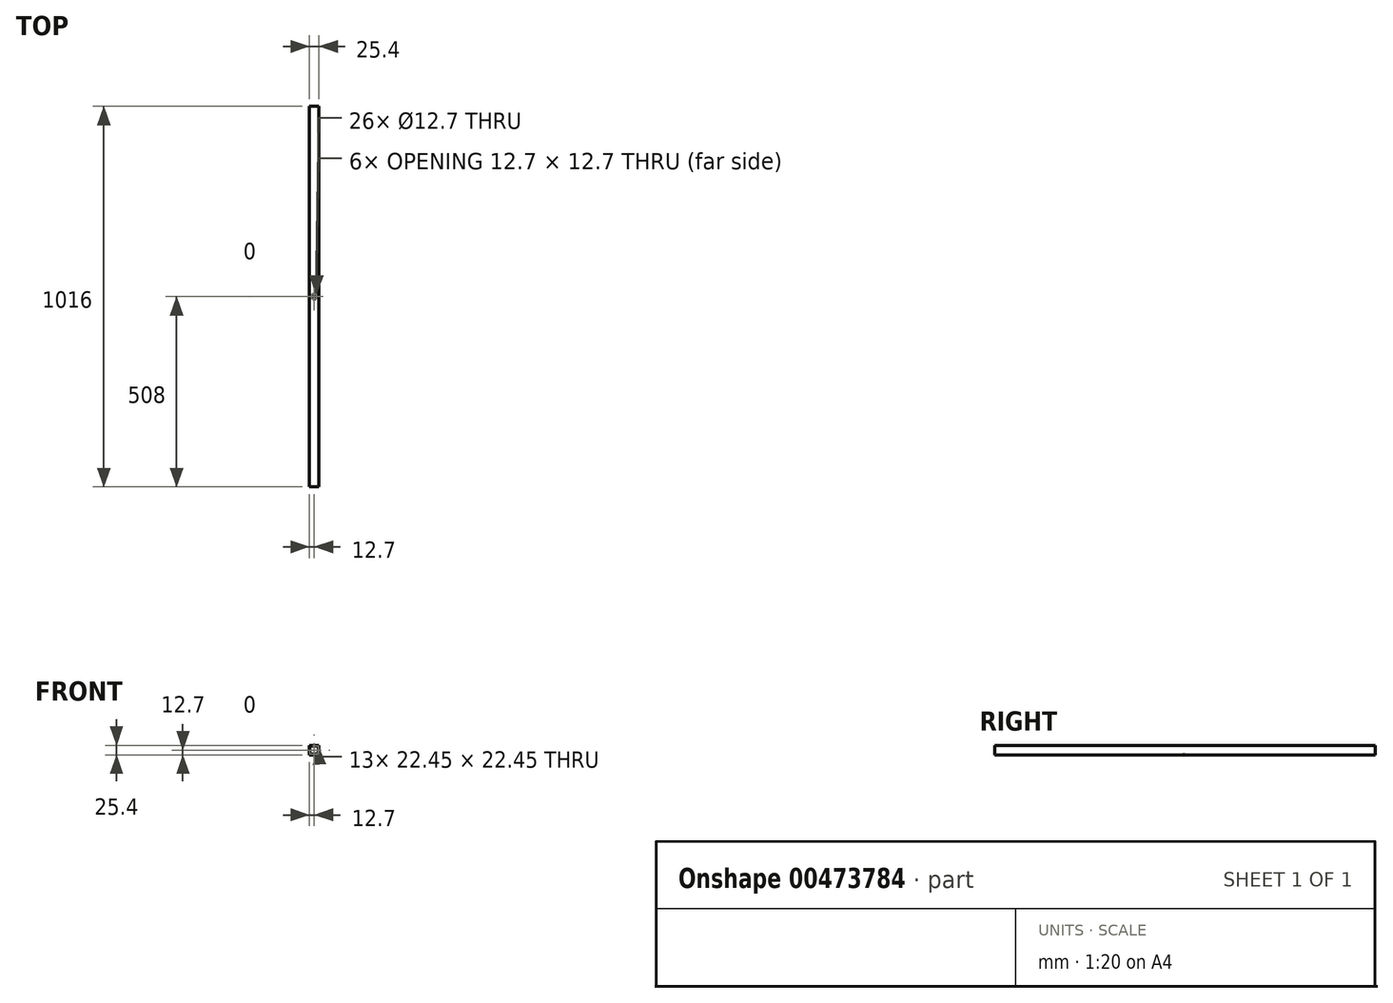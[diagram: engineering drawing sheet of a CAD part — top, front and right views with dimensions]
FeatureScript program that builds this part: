
annotation { "Feature Type Name" : "Feature", "Feature Type Description" : "" }
export const myFeature = defineFeature(function(context is Context, id is Id, definition is map)
    precondition{}
    {
        {
            var Q0;
            Q0=qCreatedBy(makeId("Front.planeOp"),FACE);
            var sketch = newSketch(context, id + "F0", { "sketchPlane" : qUnion([Q0])});
            skLineSegment(sketch, "E0.bottom", {"start": v(0, 0) * mm, "end": v(25.4, 0) * mm});
            skLineSegment(sketch, "E0.top", {"start": v(0, 25.4) * mm, "end": v(25.4, 25.4) * mm});
            skLineSegment(sketch, "E0.left", {"start": v(0, 0) * mm, "end": v(0, 25.4) * mm});
            skLineSegment(sketch, "E0.right", {"start": v(25.4, 0) * mm, "end": v(25.4, 25.4) * mm});
            skLineSegment(sketch, "E1.0", {"start": v(23.93, 1.47) * mm, "end": v(23.93, 23.93) * mm});
            skLineSegment(sketch, "E1.1", {"start": v(1.47, 1.47) * mm, "end": v(23.93, 1.47) * mm});
            skLineSegment(sketch, "E1.2", {"start": v(1.47, 1.47) * mm, "end": v(1.47, 23.93) * mm});
            skLineSegment(sketch, "E1.3", {"start": v(1.47, 23.93) * mm, "end": v(23.93, 23.93) * mm});
            skSolve(sketch);
        }
        {
            var Q0;
            Q0 = qSketchRegion(id + "F0", true);
            extrude(context, id + "F1", {"entities" : qUnion([Q0]), "depth" : 1016 * mm});
        }
        {
            var Q0;
            Q0=makeQuery(id+"F1.opExtrude","SWEPT_FACE",FACE,{"disambiguationData":[OSD([sQuery(id+"F0.wireOp",EDGE,"E0.bottom")])]});
            var sketch = newSketch(context, id + "F2", { "sketchPlane" : qUnion([Q0])});
            skLineSegment(sketch, "E2", {"start": v(0, 508) * mm, "end": v(25.4, 508) * mm, "construction": true});
            skCircle(sketch, "E3", {"center": v(12.7, 508) * mm, "radius": 6.35 * mm});
            skSolve(sketch);
        }
        {
            var Q0;
            Q0 = qSketchRegion(id + "F2", true);
            extrude(context, id + "F3", {"entities" : qUnion([Q0]), "operationType" : NewBodyOperationType.REMOVE, "endBound" : BoundingType.THROUGH_ALL, "oppositeDirection" : true, "depth" : 25.4 * mm});
        }
    });
